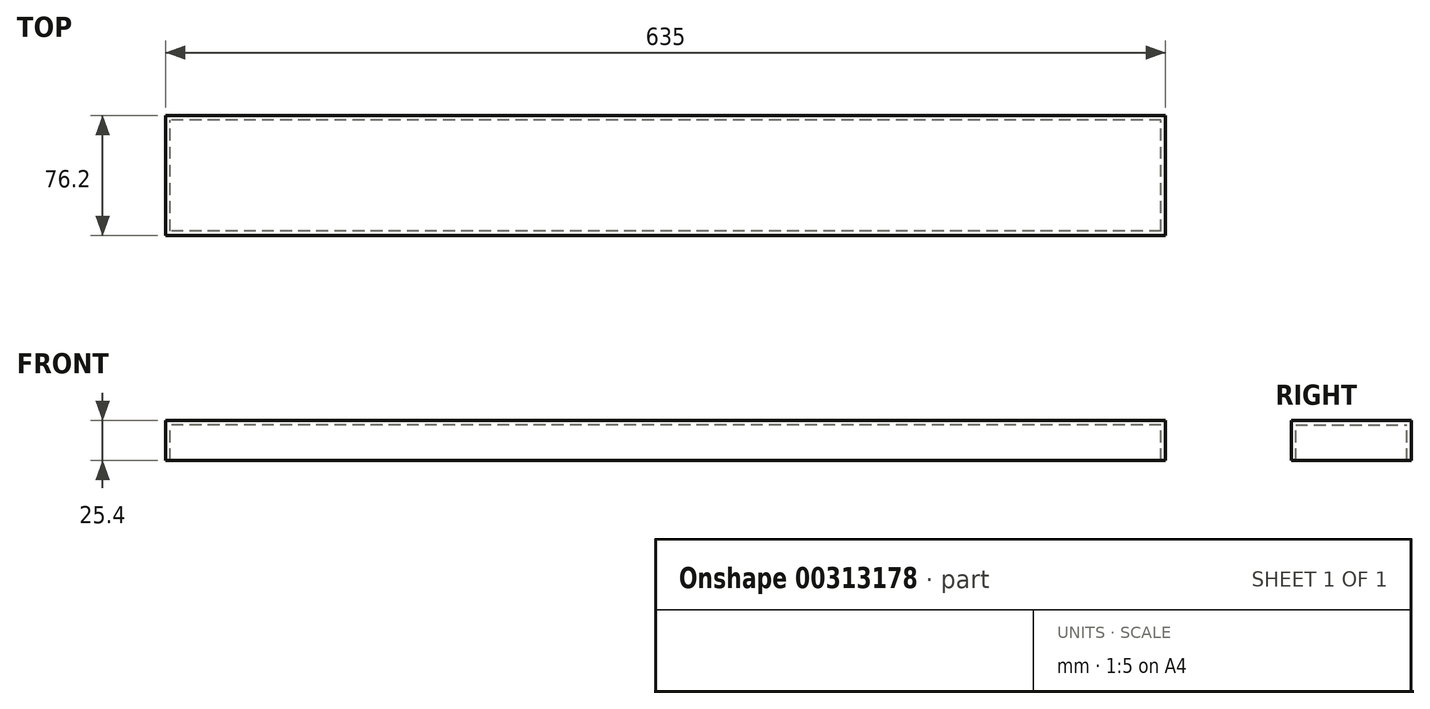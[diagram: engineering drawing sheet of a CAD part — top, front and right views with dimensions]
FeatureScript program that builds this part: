
annotation { "Feature Type Name" : "Feature", "Feature Type Description" : "" }
export const myFeature = defineFeature(function(context is Context, id is Id, definition is map)
    precondition{}
    {
        {
            var Q0;
            Q0=qCreatedBy(makeId("Right.planeOp"),FACE);
            var sketch = newSketch(context, id + "F0", { "sketchPlane" : qUnion([Q0])});
            skLineSegment(sketch, "E0.bottom", {"start": v(0, 0) * mm, "end": v(76.2, 0) * mm});
            skLineSegment(sketch, "E0.top", {"start": v(0, 25.4) * mm, "end": v(76.2, 25.4) * mm});
            skLineSegment(sketch, "E0.left", {"start": v(0, 0) * mm, "end": v(0, 25.4) * mm});
            skLineSegment(sketch, "E0.right", {"start": v(76.2, 0) * mm, "end": v(76.2, 25.4) * mm});
            skSolve(sketch);
        }
        {
            var Q0;
            Q0 = qSketchRegion(id + "F0", true);
            extrude(context, id + "F1", {"entities" : qUnion([Q0]), "endBound" : BoundingType.SYMMETRIC, "depth" : 635 * mm});
        }
        {
            var Q0;
            Q0=makeQuery(id+"F1.opExtrude","SWEPT_FACE",FACE,{"disambiguationData":[OSD([sQuery(id+"F0.wireOp",EDGE,"E0.bottom")])]});
            shell(context, id + "F2", {"entities" : qUnion([Q0]), "thickness" : 2.78 * mm});
        }
    });
